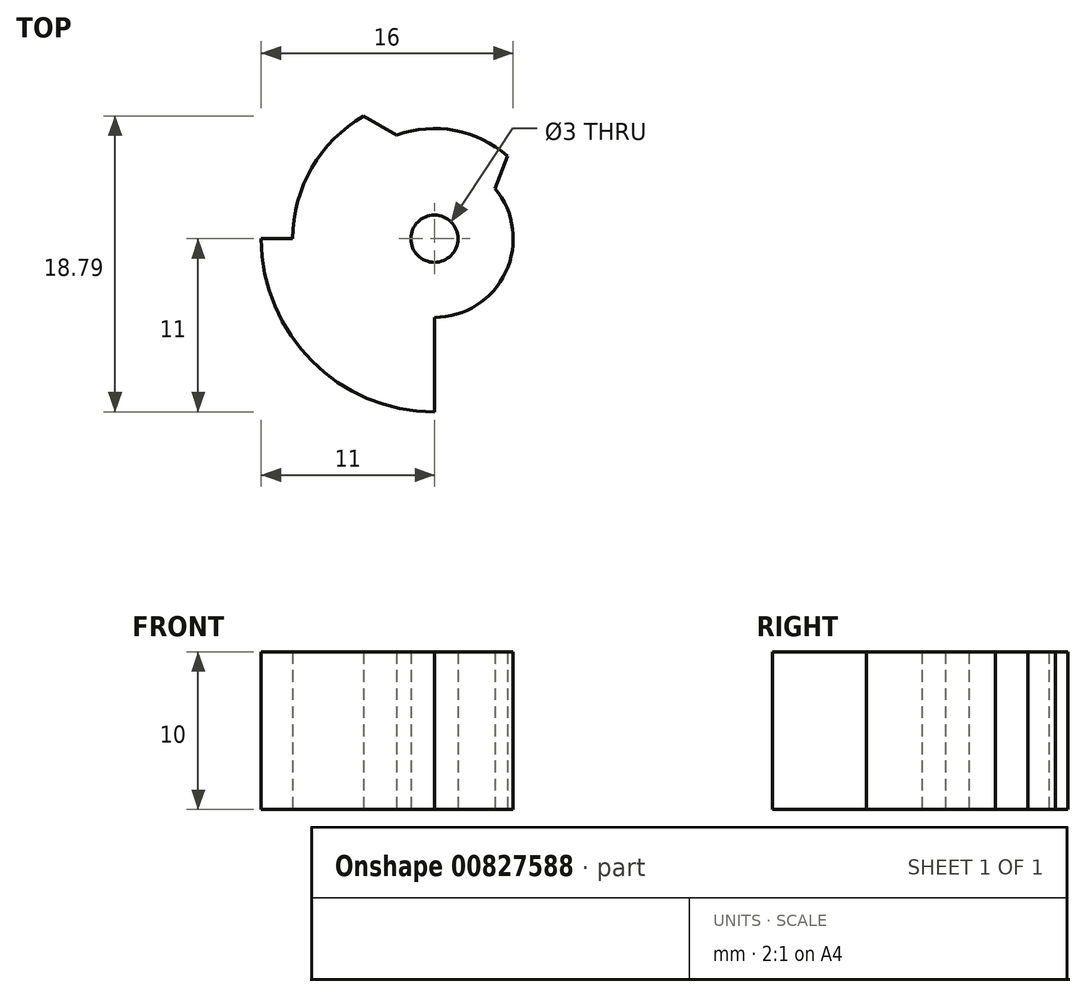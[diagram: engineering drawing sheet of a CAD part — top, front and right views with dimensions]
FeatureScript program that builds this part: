
annotation { "Feature Type Name" : "Feature", "Feature Type Description" : "" }
export const myFeature = defineFeature(function(context is Context, id is Id, definition is map)
    precondition{}
    {
        {
            var Q0;
            Q0=qCreatedBy(makeId("Top.planeOp"),FACE);
            var sketch = newSketch(context, id + "F0", { "sketchPlane" : qUnion([Q0])});
            skCircle(sketch, "E0", {"center": v(0, 0) * mm, "radius": 11 * mm});
            skCircle(sketch, "E1", {"center": v(0, 0) * mm, "radius": 1.5 * mm});
            skSolve(sketch);
        }
        {
            var Q0;
            Q0 = qSketchRegion(id + "F0", true);
            extrude(context, id + "F1", {"entities" : qUnion([Q0]), "depth" : 10 * mm, "offsetDistance" : 25 * mm});
        }
        {
            var Q0;
            Q0=makeQuery(id+"F1.opExtrude","CAP_FACE",FACE,{"disambiguationData":[OSD([sQuery(id+"F0.wireOp",EDGE,"E0"),sQuery(id+"F0.wireOp",EDGE,"E1")])],"isStart":true});
            var sketch = newSketch(context, id + "F2", { "sketchPlane" : qUnion([Q0])});
            skLineSegment(sketch, "E2", {"start": v(0, 0) * mm, "end": v(0, 11) * mm});
            skCircle(sketch, "E3", {"center": v(0, 0) * mm, "radius": 9 * mm});
            skCircle(sketch, "E4", {"center": v(0, 0) * mm, "radius": 7 * mm});
            skCircle(sketch, "E5", {"center": v(0, 0) * mm, "radius": 5 * mm});
            skLineSegment(sketch, "E6", {"start": v(-11, 0) * mm, "end": v(-9, 0) * mm});
            skLineSegment(sketch, "E7", {"start": v(0, -11) * mm, "end": v(0, -7) * mm});
            skLineSegment(sketch, "E8", {"start": v(5, 0) * mm, "end": v(11, 0) * mm});
            skSolve(sketch);
        }
        {
            var Q0;
            {var subQ0=sQuery(id+"F2.wireOp",EDGE,"E6");Q0=makeQuery(id+"F2.imprint","IMPRINT",FACE,{"disambiguationData":[TD([[makeQuery(id+"F2.imprint","IMPRINT",EDGE,{"derivedFrom":subQ0}),-1.0]])]});}
            var Q1;
            {var subQ0=sQuery(id+"F2.wireOp",EDGE,"E8");var subQ1=sQuery(id+"F2.wireOp",EDGE,"E3");var subQ2=makeQuery(id+"F2.imprint","INTERSECT",VERTEX,{"derivedFrom":[subQ1,subQ0]});Q1=makeQuery(id+"F2.imprint","IMPRINT",FACE,{"disambiguationData":[TD([[makeQuery(id+"F2.imprint","IMPRINT",EDGE,{"disambiguationData":[TD([[subQ2,1.0]])],"derivedFrom":subQ1}),-1.0]])]});}
            var Q2;
            {var subQ0=sQuery(id+"F2.wireOp",EDGE,"E8");var subQ1=sQuery(id+"F2.wireOp",EDGE,"E3");var subQ2=makeQuery(id+"F2.imprint","INTERSECT",VERTEX,{"derivedFrom":[subQ1,subQ0]});Q2=makeQuery(id+"F2.imprint","IMPRINT",FACE,{"disambiguationData":[TD([[makeQuery(id+"F2.imprint","IMPRINT",EDGE,{"disambiguationData":[TD([[subQ2,1.0]])],"derivedFrom":subQ1}),1.0]])]});}
            var Q3;
            {var subQ0=sQuery(id+"F2.wireOp",EDGE,"E5");var subQ1=sQuery(id+"F2.wireOp",EDGE,"E2");var subQ2=makeQuery(id+"F2.imprint","INTERSECT",VERTEX,{"derivedFrom":[subQ1,subQ0]});Q3=makeQuery(id+"F2.imprint","IMPRINT",FACE,{"disambiguationData":[TD([[makeQuery(id+"F2.imprint","IMPRINT",EDGE,{"disambiguationData":[TD([[subQ2,-1.0]])],"derivedFrom":subQ1}),-1.0]])]});}
            var Q4;
            {var subQ0=sQuery(id+"F2.wireOp",EDGE,"E4");var subQ1=sQuery(id+"F2.wireOp",EDGE,"E2");var subQ2=makeQuery(id+"F2.imprint","INTERSECT",VERTEX,{"derivedFrom":[subQ1,subQ0]});Q4=makeQuery(id+"F2.imprint","IMPRINT",FACE,{"disambiguationData":[TD([[makeQuery(id+"F2.imprint","IMPRINT",EDGE,{"disambiguationData":[TD([[subQ2,-1.0]])],"derivedFrom":subQ1}),-1.0]])]});}
            var Q5;
            {var subQ0=sQuery(id+"F2.wireOp",EDGE,"E2");var subQ1=makeQuery(id+"F1.opExtrude","CAP_EDGE",EDGE,{"disambiguationData":[OSD([sQuery(id+"F0.wireOp",EDGE,"E0")])],"isStart":true});var subQ2=makeQuery(id+"F2.imprint","INTERSECT",VERTEX,{"derivedFrom":[subQ1,subQ0]});Q5=makeQuery(id+"F2.imprint","IMPRINT",FACE,{"disambiguationData":[TD([[makeQuery(id+"F2.imprint","IMPRINT",EDGE,{"disambiguationData":[TD([[subQ2,1.0]])],"derivedFrom":subQ0}),-1.0]])]});}
            extrude(context, id + "F3", {"entities" : qUnion([Q0, Q1, Q2, Q3, Q4, Q5]), "operationType" : NewBodyOperationType.REMOVE, "oppositeDirection" : true, "depth" : 25 * mm, "offsetDistance" : 25 * mm});
        }
        {
            var Q0;
            Q0=makeQuery(id+"F3.boolean.opBoolean","COPY",EDGE,{"derivedFrom":makeQuery(id+"F3.opExtrude","SWEPT_EDGE",EDGE,{"disambiguationData":[OSD([sQuery(id+"F0.wireOp",EDGE,"E0"),sQuery(id+"F2.wireOp",EDGE,"E6")])]})});
            var Q1;
            Q1=makeQuery(id+"F3.boolean.opBoolean","COPY",EDGE,{"derivedFrom":makeQuery(id+"F3.opExtrude","SWEPT_EDGE",EDGE,{"disambiguationData":[OSD([sQuery(id+"F2.wireOp",EDGE,"E3"),sQuery(id+"F2.wireOp",EDGE,"E7")])]})});
            var Q2;
            Q2=makeQuery(id+"F3.boolean.opBoolean","COPY",EDGE,{"derivedFrom":makeQuery(id+"F3.opExtrude","SWEPT_EDGE",EDGE,{"disambiguationData":[OSD([sQuery(id+"F2.wireOp",EDGE,"E4"),sQuery(id+"F2.wireOp",EDGE,"E8")])]})});
            chamfer(context, id + "F4", {"entities" : qUnion([Q0, Q1, Q2]), "width" : 3 * mm, "tangentPropagation" : true});
        }
    });
